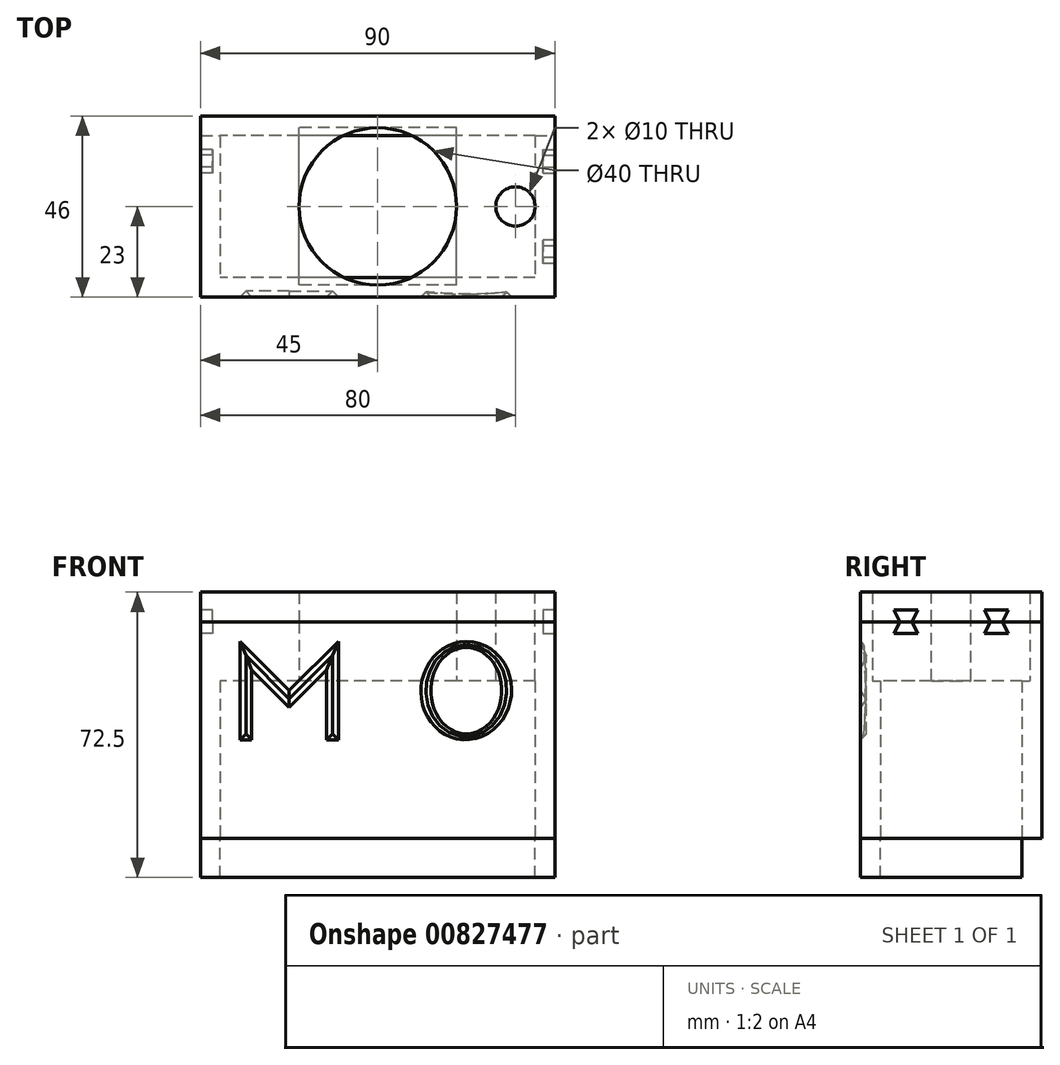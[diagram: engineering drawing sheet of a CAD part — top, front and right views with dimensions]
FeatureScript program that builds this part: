
annotation { "Feature Type Name" : "Feature", "Feature Type Description" : "" }
export const myFeature = defineFeature(function(context is Context, id is Id, definition is map)
    precondition{}
    {
        {
            var Q0;
            Q0=qCreatedBy(makeId("Top.planeOp"),FACE);
            var sketch = newSketch(context, id + "F0", { "sketchPlane" : qUnion([Q0])});
            skLineSegment(sketch, "E0.bottom", {"start": v(40, 18) * mm, "end": v(-40, 18) * mm});
            skLineSegment(sketch, "E0.top", {"start": v(40, -18) * mm, "end": v(-40, -18) * mm});
            skLineSegment(sketch, "E0.left", {"start": v(40, 18) * mm, "end": v(40, -18) * mm});
            skLineSegment(sketch, "E0.right", {"start": v(-40, 18) * mm, "end": v(-40, -18) * mm});
            skPoint(sketch, "E0.middle", {"position": v(0, 0) * mm});
            skLineSegment(sketch, "E1.bottom", {"start": v(45, -23) * mm, "end": v(-45, -23) * mm});
            skLineSegment(sketch, "E1.top", {"start": v(45, 23) * mm, "end": v(-45, 23) * mm});
            skLineSegment(sketch, "E1.left", {"start": v(45, -23) * mm, "end": v(45, 23) * mm});
            skLineSegment(sketch, "E1.right", {"start": v(-45, -23) * mm, "end": v(-45, 23) * mm});
            skSolve(sketch);
        }
        {
            var Q0;
            Q0=makeQuery(id+"F0.imprint","IMPRINT",FACE,{"disambiguationData":[TD([[makeQuery(id+"F0.imprint","IMPRINT",EDGE,{"derivedFrom":sQuery(id+"F0.wireOp",EDGE,"E0.bottom")}),-1.0]])]});
            extrude(context, id + "F1", {"entities" : qUnion([Q0]), "depth" : 40 * mm, "offsetDistance" : 25 * mm});
        }
        {
            var Q0;
            Q0=makeQuery(id+"F1.opExtrude","CAP_FACE",FACE,{"disambiguationData":[OSD([sQuery(id+"F0.wireOp",EDGE,"E0.bottom"),sQuery(id+"F0.wireOp",EDGE,"E0.top"),sQuery(id+"F0.wireOp",EDGE,"E0.left"),sQuery(id+"F0.wireOp",EDGE,"E0.right"),sQuery(id+"F0.wireOp",EDGE,"E1.bottom"),sQuery(id+"F0.wireOp",EDGE,"E1.top"),sQuery(id+"F0.wireOp",EDGE,"E1.left"),sQuery(id+"F0.wireOp",EDGE,"E1.right")])],"isStart":false});
            var sketch = newSketch(context, id + "F2", { "sketchPlane" : qUnion([Q0])});
            skLineSegment(sketch, "E2.bottom", {"start": v(20, -20) * mm, "end": v(-20, -20) * mm});
            skLineSegment(sketch, "E2.top", {"start": v(20, 20) * mm, "end": v(-20, 20) * mm});
            skLineSegment(sketch, "E2.left", {"start": v(20, -20) * mm, "end": v(20, 20) * mm});
            skLineSegment(sketch, "E2.right", {"start": v(-20, -20) * mm, "end": v(-20, 20) * mm});
            skPoint(sketch, "E2.middle", {"position": v(0, 0) * mm});
            skLineSegment(sketch, "E3.bottom", {"start": v(-45, 23) * mm, "end": v(45, 23) * mm});
            skLineSegment(sketch, "E3.top", {"start": v(-45, -23) * mm, "end": v(45, -23) * mm});
            skLineSegment(sketch, "E3.left", {"start": v(-45, 23) * mm, "end": v(-45, -23) * mm});
            skLineSegment(sketch, "E3.right", {"start": v(45, 23) * mm, "end": v(45, -23) * mm});
            skSolve(sketch);
        }
        {
            var Q0;
            {var subQ5=makeQuery(id+"F1.opExtrude","CAP_EDGE",EDGE,{"disambiguationData":[OSD([sQuery(id+"F0.wireOp",EDGE,"E0.right")])],"isStart":false});Q0=makeQuery(id+"F2.imprint","IMPRINT",FACE,{"disambiguationData":[TD([[makeQuery(id+"F2.imprint","IMPRINT",EDGE,{"derivedFrom":subQ5}),1.0]])]});}
            var Q1;
            {var subQ5=makeQuery(id+"F1.opExtrude","CAP_EDGE",EDGE,{"disambiguationData":[OSD([sQuery(id+"F0.wireOp",EDGE,"E0.left")])],"isStart":false});Q1=makeQuery(id+"F2.imprint","IMPRINT",FACE,{"disambiguationData":[TD([[makeQuery(id+"F2.imprint","IMPRINT",EDGE,{"derivedFrom":subQ5}),-1.0]])]});}
            var Q2;
            {var subQ4=sQuery(id+"F2.wireOp",EDGE,"E2.bottom");Q2=makeQuery(id+"F2.imprint","IMPRINT",FACE,{"disambiguationData":[TD([[makeQuery(id+"F2.imprint","IMPRINT",EDGE,{"derivedFrom":subQ4}),1.0]])]});}
            extrude(context, id + "F3", {"entities" : qUnion([Q0, Q1, Q2]), "operationType" : NewBodyOperationType.ADD, "depth" : 15 * mm, "offsetDistance" : 25 * mm});
        }
        {
            var Q0;
            Q0=makeQuery(id+"F3.opExtrude","CAP_FACE",FACE,{"disambiguationData":[OSD([sQuery(id+"F2.wireOp",EDGE,"E2.bottom"),sQuery(id+"F2.wireOp",EDGE,"E2.top"),sQuery(id+"F2.wireOp",EDGE,"E2.left"),sQuery(id+"F2.wireOp",EDGE,"E2.right"),sQuery(id+"F2.wireOp",EDGE,"E3.bottom"),sQuery(id+"F2.wireOp",EDGE,"E3.top"),sQuery(id+"F2.wireOp",EDGE,"E3.left"),sQuery(id+"F2.wireOp",EDGE,"E3.right")])],"isStart":false});
            var sketch = newSketch(context, id + "F4", { "sketchPlane" : qUnion([Q0])});
            skCircle(sketch, "E4", {"center": v(0, 0) * mm, "radius": 20 * mm});
            skLineSegment(sketch, "E5.bottom", {"start": v(-45, 23) * mm, "end": v(45, 23) * mm});
            skLineSegment(sketch, "E5.top", {"start": v(-45, -23) * mm, "end": v(45, -23) * mm});
            skLineSegment(sketch, "E5.left", {"start": v(-45, 23) * mm, "end": v(-45, -23) * mm});
            skLineSegment(sketch, "E5.right", {"start": v(45, 23) * mm, "end": v(45, -23) * mm});
            skSolve(sketch);
        }
        {
            var Q0;
            Q0 = qSketchRegion(id + "F4", true);
            extrude(context, id + "F5", {"entities" : qUnion([Q0]), "depth" : 7.5 * mm, "offsetDistance" : 25 * mm});
        }
        {
            var Q0;
            Q0=makeQuery(id+"F3.boolean.opBoolean","MERGE",FACE,{"derivedFrom":[makeQuery(id+"F1.opExtrude","SWEPT_FACE",FACE,{"disambiguationData":[OSD([sQuery(id+"F0.wireOp",EDGE,"E1.right")])]}),makeQuery(id+"F3.opExtrude","SWEPT_FACE",FACE,{"disambiguationData":[OSD([sQuery(id+"F2.wireOp",EDGE,"E3.left")])]})]});
            var sketch = newSketch(context, id + "F6", { "sketchPlane" : qUnion([Q0])});
            skLineSegment(sketch, "E6", {"start": v(-13, 55) * mm, "end": v(-10, 55) * mm});
            skLineSegment(sketch, "E7", {"start": v(-10, 55) * mm, "end": v(-8.5, 58) * mm});
            skLineSegment(sketch, "E8", {"start": v(-8.5, 58) * mm, "end": v(-14.5, 58) * mm});
            skLineSegment(sketch, "E9", {"start": v(-14.5, 58) * mm, "end": v(-13, 55) * mm});
            skLineSegment(sketch, "E10", {"start": v(-13, 55) * mm, "end": v(-14.5, 52) * mm});
            skLineSegment(sketch, "E11", {"start": v(-14.5, 52) * mm, "end": v(-8.5, 52) * mm});
            skLineSegment(sketch, "E12", {"start": v(-8.5, 52) * mm, "end": v(-10, 55) * mm});
            skLineSegment(sketch, "E13", {"start": v(-11.5, 55) * mm, "end": v(-11.5, 52) * mm, "construction": true});
            skLineSegment(sketch, "E14", {"start": v(-11.5, 55) * mm, "end": v(-11.5, 58) * mm, "construction": true});
            skLineSegment(sketch, "E15", {"start": v(0, 55) * mm, "end": v(-23, 55) * mm});
            skLineSegment(sketch, "E16", {"start": v(0, 55) * mm, "end": v(23, 55) * mm});
            skLineSegment(sketch, "E17", {"start": v(10, 55) * mm, "end": v(13, 55) * mm});
            skLineSegment(sketch, "E18", {"start": v(13, 55) * mm, "end": v(14.5, 58) * mm});
            skLineSegment(sketch, "E19", {"start": v(14.5, 58) * mm, "end": v(8.5, 58) * mm});
            skLineSegment(sketch, "E20", {"start": v(8.5, 58) * mm, "end": v(10, 55) * mm});
            skLineSegment(sketch, "E21", {"start": v(10, 55) * mm, "end": v(8.5, 52) * mm});
            skLineSegment(sketch, "E22", {"start": v(8.5, 52) * mm, "end": v(14.5, 52) * mm});
            skLineSegment(sketch, "E23", {"start": v(14.5, 52) * mm, "end": v(13, 55) * mm});
            skLineSegment(sketch, "E24", {"start": v(11.5, 55) * mm, "end": v(11.5, 52) * mm, "construction": true});
            skLineSegment(sketch, "E25", {"start": v(11.5, 55) * mm, "end": v(11.5, 58) * mm, "construction": true});
            skSolve(sketch);
        }
        {
            var Q0;
            {var subQ0=sQuery(id+"F6.wireOp",EDGE,"E7");Q0=makeQuery(id+"F6.imprint","IMPRINT",FACE,{"disambiguationData":[TD([[makeQuery(id+"F6.imprint","IMPRINT",EDGE,{"derivedFrom":subQ0}),1.0]])]});}
            var Q1;
            {var subQ0=sQuery(id+"F6.wireOp",EDGE,"E10");Q1=makeQuery(id+"F6.imprint","IMPRINT",FACE,{"disambiguationData":[TD([[makeQuery(id+"F6.imprint","IMPRINT",EDGE,{"derivedFrom":subQ0}),1.0]])]});}
            var Q2;
            Q2=makeQuery(id+"F6.imprint","IMPRINT",FACE,{"disambiguationData":[TD([[makeQuery(id+"F6.imprint","IMPRINT",EDGE,{"derivedFrom":sQuery(id+"F6.wireOp",EDGE,"E17")}),-1.0]])]});
            var Q3;
            Q3=makeQuery(id+"F6.imprint","IMPRINT",FACE,{"disambiguationData":[TD([[makeQuery(id+"F6.imprint","IMPRINT",EDGE,{"derivedFrom":sQuery(id+"F6.wireOp",EDGE,"E17")}),1.0]])]});
            extrude(context, id + "F7", {"entities" : qUnion([Q0, Q1, Q2, Q3]), "operationType" : NewBodyOperationType.REMOVE, "oppositeDirection" : true, "depth" : 3 * mm, "offsetDistance" : 25 * mm});
        }
        {
            var Q0;
            Q0=makeQuery(id+"F3.boolean.opBoolean","MERGE",FACE,{"derivedFrom":[makeQuery(id+"F1.opExtrude","SWEPT_FACE",FACE,{"disambiguationData":[OSD([sQuery(id+"F0.wireOp",EDGE,"E1.left")])]}),makeQuery(id+"F3.opExtrude","SWEPT_FACE",FACE,{"disambiguationData":[OSD([sQuery(id+"F2.wireOp",EDGE,"E3.right")])]})]});
            var sketch = newSketch(context, id + "F8", { "sketchPlane" : qUnion([Q0])});
            skLineSegment(sketch, "E26", {"start": v(10, 55) * mm, "end": v(13, 55) * mm});
            skLineSegment(sketch, "E27", {"start": v(13, 55) * mm, "end": v(14.5, 58) * mm});
            skLineSegment(sketch, "E28", {"start": v(14.5, 58) * mm, "end": v(8.5, 58) * mm});
            skLineSegment(sketch, "E29", {"start": v(8.5, 58) * mm, "end": v(10, 55) * mm});
            skLineSegment(sketch, "E30", {"start": v(10, 55) * mm, "end": v(8.5, 52) * mm});
            skLineSegment(sketch, "E31", {"start": v(8.5, 52) * mm, "end": v(14.5, 52) * mm});
            skLineSegment(sketch, "E32", {"start": v(14.5, 52) * mm, "end": v(13, 55) * mm});
            skLineSegment(sketch, "E33", {"start": v(11.5, 55) * mm, "end": v(11.5, 52) * mm, "construction": true});
            skLineSegment(sketch, "E34", {"start": v(11.5, 55) * mm, "end": v(11.5, 58) * mm, "construction": true});
            skLineSegment(sketch, "E35", {"start": v(-13, 55) * mm, "end": v(-10, 55) * mm});
            skLineSegment(sketch, "E36", {"start": v(-10, 55) * mm, "end": v(-8.5, 58) * mm});
            skLineSegment(sketch, "E37", {"start": v(-8.5, 58) * mm, "end": v(-14.5, 58) * mm});
            skLineSegment(sketch, "E38", {"start": v(-14.5, 58) * mm, "end": v(-13, 55) * mm});
            skLineSegment(sketch, "E39", {"start": v(-13, 55) * mm, "end": v(-14.5, 52) * mm});
            skLineSegment(sketch, "E40", {"start": v(-14.5, 52) * mm, "end": v(-8.5, 52) * mm});
            skLineSegment(sketch, "E41", {"start": v(-8.5, 52) * mm, "end": v(-10, 55) * mm});
            skLineSegment(sketch, "E42", {"start": v(-11.5, 55) * mm, "end": v(-11.5, 52) * mm, "construction": true});
            skLineSegment(sketch, "E43", {"start": v(-11.5, 55) * mm, "end": v(-11.5, 58) * mm, "construction": true});
            skLineSegment(sketch, "E44", {"start": v(23, 55) * mm, "end": v(0, 55) * mm});
            skLineSegment(sketch, "E45", {"start": v(-23, 55) * mm, "end": v(0, 55) * mm});
            skSolve(sketch);
        }
        {
            var Q0;
            Q0 = qSketchRegion(id + "F8", true);
            extrude(context, id + "F9", {"entities" : qUnion([Q0]), "operationType" : NewBodyOperationType.REMOVE, "oppositeDirection" : true, "depth" : 3 * mm, "offsetDistance" : 25 * mm});
        }
        {
            var Q0;
            {var subQ0=sQuery(id+"F8.wireOp",EDGE,"E36");var subQ1=sQuery(id+"F8.wireOp",EDGE,"E37");var subQ2=sQuery(id+"F8.wireOp",EDGE,"E38");Q0=makeQuery(id+"F9.boolean.opBoolean","COPY",FACE,{"disambiguationData":[TD([makeQuery(id+"F9.opExtrude","SWEPT_FACE",FACE,{"disambiguationData":[OSD([subQ0])]})])],"derivedFrom":makeQuery(id+"F9.opExtrude","CAP_FACE",FACE,{"disambiguationData":[OSD([subQ0,subQ1,subQ2,sQuery(id+"F8.wireOp",EDGE,"E39"),sQuery(id+"F8.wireOp",EDGE,"E40"),sQuery(id+"F8.wireOp",EDGE,"E41")])],"isStart":false})});}
            var Q1;
            {var subQ0=sQuery(id+"F8.wireOp",EDGE,"E39");var subQ1=sQuery(id+"F8.wireOp",EDGE,"E40");var subQ2=sQuery(id+"F8.wireOp",EDGE,"E41");Q1=makeQuery(id+"F9.boolean.opBoolean","COPY",FACE,{"disambiguationData":[TD([makeQuery(id+"F9.opExtrude","SWEPT_FACE",FACE,{"disambiguationData":[OSD([subQ0])]})])],"derivedFrom":makeQuery(id+"F9.opExtrude","CAP_FACE",FACE,{"disambiguationData":[OSD([sQuery(id+"F8.wireOp",EDGE,"E36"),sQuery(id+"F8.wireOp",EDGE,"E37"),sQuery(id+"F8.wireOp",EDGE,"E38"),subQ0,subQ1,subQ2])],"isStart":false})});}
            var Q2;
            Q2=makeQuery(id+"F3.boolean.opBoolean","MERGE",FACE,{"derivedFrom":[makeQuery(id+"F1.opExtrude","SWEPT_FACE",FACE,{"disambiguationData":[OSD([sQuery(id+"F0.wireOp",EDGE,"E1.left")])]}),makeQuery(id+"F3.opExtrude","SWEPT_FACE",FACE,{"disambiguationData":[OSD([sQuery(id+"F2.wireOp",EDGE,"E3.right")])]})]});
            extrude(context, id + "F10", {"entities" : qUnion([Q0, Q1]), "endBound" : BoundingType.UP_TO_SURFACE, "depth" : 25 * mm, "endBoundEntityFace" : qUnion([Q2]), "offsetDistance" : 25 * mm});
        }
        {
            var Q0;
            Q0=makeQuery(id+"F1.opExtrude","CAP_FACE",FACE,{"disambiguationData":[OSD([sQuery(id+"F0.wireOp",EDGE,"E0.bottom"),sQuery(id+"F0.wireOp",EDGE,"E0.top"),sQuery(id+"F0.wireOp",EDGE,"E0.left"),sQuery(id+"F0.wireOp",EDGE,"E0.right"),sQuery(id+"F0.wireOp",EDGE,"E1.bottom"),sQuery(id+"F0.wireOp",EDGE,"E1.top"),sQuery(id+"F0.wireOp",EDGE,"E1.left"),sQuery(id+"F0.wireOp",EDGE,"E1.right")])],"isStart":true});
            var sketch = newSketch(context, id + "F11", { "sketchPlane" : qUnion([Q0])});
            skLineSegment(sketch, "E46", {"start": v(45, -18) * mm, "end": v(45, 23) * mm});
            skLineSegment(sketch, "E47", {"start": v(45, 23) * mm, "end": v(-45, 23) * mm});
            skLineSegment(sketch, "E48", {"start": v(-45, 23) * mm, "end": v(-45, -18) * mm});
            skLineSegment(sketch, "E49", {"start": v(-45, -18) * mm, "end": v(-40, -18) * mm});
            skLineSegment(sketch, "E50", {"start": v(-40, -18) * mm, "end": v(-40, 18) * mm});
            skLineSegment(sketch, "E51", {"start": v(-40, 18) * mm, "end": v(40, 18) * mm});
            skLineSegment(sketch, "E52", {"start": v(40, 18) * mm, "end": v(40, -18) * mm});
            skLineSegment(sketch, "E53", {"start": v(40, -18) * mm, "end": v(45, -18) * mm});
            skSolve(sketch);
        }
        {
            var Q0;
            Q0 = qSketchRegion(id + "F11", true);
            extrude(context, id + "F12", {"entities" : qUnion([Q0]), "depth" : 10 * mm, "offsetDistance" : 25 * mm});
        }
        {
            var Q0;
            Q0=makeQuery(id+"F5.opExtrude","CAP_FACE",FACE,{"disambiguationData":[OSD([sQuery(id+"F4.wireOp",EDGE,"E4"),sQuery(id+"F4.wireOp",EDGE,"E5.bottom"),sQuery(id+"F4.wireOp",EDGE,"E5.top"),sQuery(id+"F4.wireOp",EDGE,"E5.left"),sQuery(id+"F4.wireOp",EDGE,"E5.right")])],"isStart":false});
            var sketch = newSketch(context, id + "F13", { "sketchPlane" : qUnion([Q0])});
            skCircle(sketch, "E54", {"center": v(35, 0) * mm, "radius": 5 * mm});
            skSolve(sketch);
        }
        {
            var Q0;
            Q0=makeQuery(id+"F13.imprint","IMPRINT",FACE,{"disambiguationData":[TD([[makeQuery(id+"F13.imprint","IMPRINT",EDGE,{"derivedFrom":sQuery(id+"F13.wireOp",EDGE,"E54")}),1.0]])]});
            var Q1;
            {var subQ1=sQuery(id+"F0.wireOp",EDGE,"E0.right");var subQ3=sQuery(id+"F2.wireOp",EDGE,"E2.right");Q1=makeQuery(id+"F3.boolean.opBoolean","SPLIT",FACE,{"disambiguationData":[TD([makeQuery(id+"F1.opExtrude","SWEPT_FACE",FACE,{"disambiguationData":[OSD([subQ1])]})])],"derivedFrom":makeQuery(id+"F3.opExtrude","CAP_FACE",FACE,{"disambiguationData":[OSD([sQuery(id+"F2.wireOp",EDGE,"E2.bottom"),sQuery(id+"F2.wireOp",EDGE,"E2.top"),sQuery(id+"F2.wireOp",EDGE,"E2.left"),subQ3,sQuery(id+"F2.wireOp",EDGE,"E3.bottom"),sQuery(id+"F2.wireOp",EDGE,"E3.top"),sQuery(id+"F2.wireOp",EDGE,"E3.left"),sQuery(id+"F2.wireOp",EDGE,"E3.right")])],"isStart":true})});}
            extrude(context, id + "F14", {"entities" : qUnion([Q0]), "operationType" : NewBodyOperationType.REMOVE, "endBound" : BoundingType.THROUGH_ALL, "oppositeDirection" : true, "depth" : 25 * mm, "endBoundEntityFace" : qUnion([Q1]), "offsetDistance" : 25 * mm});
        }
        {
            var Q0;
            Q0=makeQuery(id+"F3.boolean.opBoolean","MERGE",FACE,{"derivedFrom":[makeQuery(id+"F1.opExtrude","SWEPT_FACE",FACE,{"disambiguationData":[OSD([sQuery(id+"F0.wireOp",EDGE,"E1.bottom")])]}),makeQuery(id+"F3.opExtrude","SWEPT_FACE",FACE,{"disambiguationData":[OSD([sQuery(id+"F2.wireOp",EDGE,"E3.top")])]})]});
            var sketch = newSketch(context, id + "F15", { "sketchPlane" : qUnion([Q0])});
            skLineSegment(sketch, "E55", {"start": v(-35, 25) * mm, "end": v(-35, 50) * mm});
            skLineSegment(sketch, "E56", {"start": v(-35, 50) * mm, "end": v(-22.5, 37.5) * mm});
            skLineSegment(sketch, "E57", {"start": v(-22.5, 37.5) * mm, "end": v(-10, 50) * mm});
            skLineSegment(sketch, "E58", {"start": v(-10, 50) * mm, "end": v(-10, 25) * mm});
            skLineSegment(sketch, "E59", {"start": v(-35, 25) * mm, "end": v(-32, 25) * mm});
            skLineSegment(sketch, "E60", {"start": v(-32, 25) * mm, "end": v(-32, 42.76) * mm});
            skLineSegment(sketch, "E61", {"start": v(-32, 42.76) * mm, "end": v(-22.5, 33.26) * mm});
            skLineSegment(sketch, "E62", {"start": v(-22.5, 33.26) * mm, "end": v(-13, 42.76) * mm});
            skLineSegment(sketch, "E63", {"start": v(-13, 42.76) * mm, "end": v(-13, 25) * mm});
            skLineSegment(sketch, "E64", {"start": v(-13, 25) * mm, "end": v(-10, 25) * mm});
            skEllipse(sketch, "E65", {"center": v(22.5, 37.5) * mm, "majorRadius": 11 * mm, "minorRadius": 9 * mm, "majorAxis": v(0, 1)});
            skEllipse(sketch, "E66", {"center": v(22.5, 37.5) * mm, "majorRadius": 12.5 * mm, "minorRadius": 11.5 * mm, "majorAxis": v(0.07, 1)});
            skLineSegment(sketch, "E67", {"start": v(0, 0) * mm, "end": v(0, 55) * mm});
            skLineSegment(sketch, "E68", {"start": v(-22.5, 33.26) * mm, "end": v(-22.5, 37.5) * mm});
            skLineSegment(sketch, "E69", {"start": v(0, 27.5) * mm, "end": v(-45, 27.5) * mm});
            skLineSegment(sketch, "E70", {"start": v(0, 27.5) * mm, "end": v(45, 27.5) * mm});
            skLineSegment(sketch, "E71", {"start": v(22.5, 27.5) * mm, "end": v(22.5, 32.29) * mm});
            skLineSegment(sketch, "E72", {"start": v(-22.5, 27.5) * mm, "end": v(-22.5, 29.54) * mm});
            skSolve(sketch);
        }
        {
            var Q0;
            {var subQ6=sQuery(id+"F15.wireOp",EDGE,"E56");Q0=makeQuery(id+"F15.imprint","IMPRINT",FACE,{"disambiguationData":[TD([[makeQuery(id+"F15.imprint","IMPRINT",EDGE,{"derivedFrom":subQ6}),-1.0]])]});}
            var Q1;
            {var subQ0=sQuery(id+"F15.wireOp",EDGE,"E59");Q1=makeQuery(id+"F15.imprint","IMPRINT",FACE,{"disambiguationData":[TD([[makeQuery(id+"F15.imprint","IMPRINT",EDGE,{"derivedFrom":subQ0}),1.0]])]});}
            var Q2;
            {var subQ0=sQuery(id+"F15.wireOp",EDGE,"E68");Q2=makeQuery(id+"F15.imprint","IMPRINT",FACE,{"disambiguationData":[TD([[makeQuery(id+"F15.imprint","IMPRINT",EDGE,{"derivedFrom":subQ0}),1.0]])]});}
            var Q3;
            {var subQ0=sQuery(id+"F15.wireOp",EDGE,"E68");Q3=makeQuery(id+"F15.imprint","IMPRINT",FACE,{"disambiguationData":[TD([[makeQuery(id+"F15.imprint","IMPRINT",EDGE,{"derivedFrom":subQ0}),-1.0]])]});}
            var Q4;
            {var subQ6=sQuery(id+"F15.wireOp",EDGE,"E57");Q4=makeQuery(id+"F15.imprint","IMPRINT",FACE,{"disambiguationData":[TD([[makeQuery(id+"F15.imprint","IMPRINT",EDGE,{"derivedFrom":subQ6}),-1.0]])]});}
            var Q5;
            {var subQ0=sQuery(id+"F15.wireOp",EDGE,"E64");Q5=makeQuery(id+"F15.imprint","IMPRINT",FACE,{"disambiguationData":[TD([[makeQuery(id+"F15.imprint","IMPRINT",EDGE,{"derivedFrom":subQ0}),1.0]])]});}
            var Q6;
            {var subQ0=sQuery(id+"F15.wireOp",EDGE,"E70");var subQ1=sQuery(id+"F15.wireOp",EDGE,"E65");var subQ2=makeQuery(id+"F15.imprint","INTERSECT",VERTEX,{"disambiguationData":[OD(0.0)],"derivedFrom":[subQ1,subQ0]});Q6=makeQuery(id+"F15.imprint","IMPRINT",FACE,{"disambiguationData":[TD([[makeQuery(id+"F15.imprint","IMPRINT",EDGE,{"disambiguationData":[TD([[subQ2,-1.0]])],"derivedFrom":subQ1}),-1.0]])]});}
            var Q7;
            {var subQ0=sQuery(id+"F15.wireOp",EDGE,"E70");var subQ1=sQuery(id+"F15.wireOp",EDGE,"E65");var subQ2=makeQuery(id+"F15.imprint","INTERSECT",VERTEX,{"disambiguationData":[OD(0.0)],"derivedFrom":[subQ1,subQ0]});Q7=makeQuery(id+"F15.imprint","IMPRINT",FACE,{"disambiguationData":[TD([[makeQuery(id+"F15.imprint","IMPRINT",EDGE,{"disambiguationData":[TD([[subQ2,1.0]])],"derivedFrom":subQ1}),-1.0]])]});}
            extrude(context, id + "F16", {"entities" : qUnion([Q0, Q1, Q2, Q3, Q4, Q5, Q6, Q7]), "operationType" : NewBodyOperationType.REMOVE, "oppositeDirection" : true, "depth" : 2 * mm, "offsetDistance" : 25 * mm, "hasDraft" : true, "draftAngle" : 45 * degree, "draftPullDirection" : true});
        }
    });
